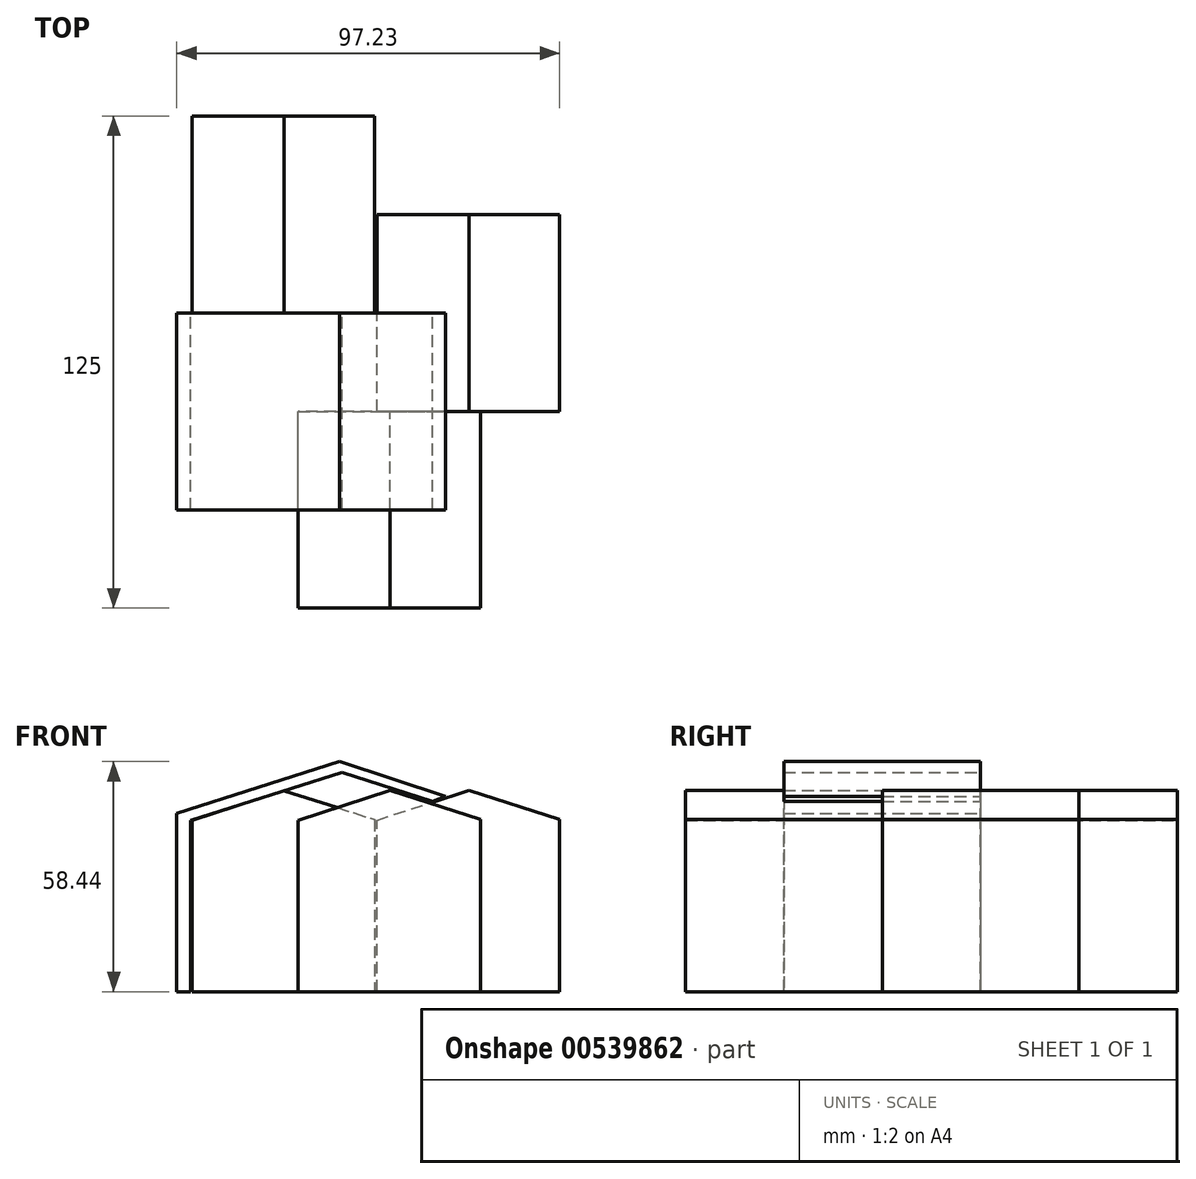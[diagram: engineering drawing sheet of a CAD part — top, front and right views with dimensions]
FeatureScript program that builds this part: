
annotation { "Feature Type Name" : "Feature", "Feature Type Description" : "" }
export const myFeature = defineFeature(function(context is Context, id is Id, definition is map)
    precondition{}
    {
        {
            var Q0;
            Q0=qCreatedBy(makeId("Front.planeOp"),FACE);
            var sketch = newSketch(context, id + "F0", { "sketchPlane" : qUnion([Q0])});
            skLineSegment(sketch, "E0", {"start": v(0, 0) * mm, "end": v(0, 43.57) * mm});
            skLineSegment(sketch, "E1", {"start": v(0, 43.57) * mm, "end": v(23.35, 51.09) * mm});
            skLineSegment(sketch, "E2", {"start": v(23.35, 51.09) * mm, "end": v(46.37, 43.73) * mm});
            skLineSegment(sketch, "E3", {"start": v(46.37, 43.73) * mm, "end": v(46.37, 0) * mm});
            skLineSegment(sketch, "E4", {"start": v(46.37, 0) * mm, "end": v(0, 0) * mm});
            skSolve(sketch);
        }
        {
            var Q0;
            Q0 = qSketchRegion(id + "F0", true);
            extrude(context, id + "F1", {"entities" : qUnion([Q0]), "depth" : 50 * mm, "offsetDistance" : 25 * mm});
        }
        {
            var Q0;
            Q0=makeQuery(id+"F1.opExtrude","SWEPT_BODY",BODY,{"disambiguationData":[OSD([sQuery(id+"F0.wireOp",EDGE,"E0"),sQuery(id+"F0.wireOp",EDGE,"E1"),sQuery(id+"F0.wireOp",EDGE,"E2"),sQuery(id+"F0.wireOp",EDGE,"E3"),sQuery(id+"F0.wireOp",EDGE,"E4")])]});
            transform(context, id + "F2", {"entities" : qUnion([Q0]), "transformType" : TransformType.TRANSLATION_3D, "dx" : 0 * mm, "dy" : 0 * mm, "dz" : 0 * mm, "makeCopy" : true});
        }
        {
            var Q0;
            Q0=makeQuery(id+"F2.opPattern","COPY",BODY,{"derivedFrom":makeQuery(id+"F1.opExtrude","SWEPT_BODY",BODY,{"disambiguationData":[OSD([sQuery(id+"F0.wireOp",EDGE,"E0"),sQuery(id+"F0.wireOp",EDGE,"E1"),sQuery(id+"F0.wireOp",EDGE,"E2"),sQuery(id+"F0.wireOp",EDGE,"E3"),sQuery(id+"F0.wireOp",EDGE,"E4")])]}),"instanceName":"1"});
            deleteBodies(context, id + "F3", {"entities" : qUnion([Q0])});
        }
        {
            var Q0;
            Q0=makeQuery(id+"F1.opExtrude","SWEPT_BODY",BODY,{"disambiguationData":[OSD([sQuery(id+"F0.wireOp",EDGE,"E0"),sQuery(id+"F0.wireOp",EDGE,"E1"),sQuery(id+"F0.wireOp",EDGE,"E2"),sQuery(id+"F0.wireOp",EDGE,"E3"),sQuery(id+"F0.wireOp",EDGE,"E4")])]});
            transform(context, id + "F4", {"entities" : qUnion([Q0]), "transformType" : TransformType.TRANSLATION_3D, "dx" : 20 * mm, "dy" : 50 * mm, "dz" : 0 * mm, "makeCopy" : true});
        }
        {
            var Q0;
            Q0=makeQuery(id+"F1.opExtrude","SWEPT_BODY",BODY,{"disambiguationData":[OSD([sQuery(id+"F0.wireOp",EDGE,"E0"),sQuery(id+"F0.wireOp",EDGE,"E1"),sQuery(id+"F0.wireOp",EDGE,"E2"),sQuery(id+"F0.wireOp",EDGE,"E3"),sQuery(id+"F0.wireOp",EDGE,"E4")])]});
            transform(context, id + "F5", {"entities" : qUnion([Q0]), "transformType" : TransformType.TRANSLATION_3D, "dx" : -27 * mm, "dy" : 75 * mm, "dz" : 0 * mm, "makeCopy" : true});
        }
        {
            var Q0;
            Q0=qCreatedBy(makeId("Front.planeOp"),FACE);
            var sketch = newSketch(context, id + "F6", { "sketchPlane" : qUnion([Q0])});
            skLineSegment(sketch, "E5", {"start": v(34.06, 48.37) * mm, "end": v(37.42, 49.65) * mm});
            skLineSegment(sketch, "E6", {"start": v(37.42, 49.65) * mm, "end": v(10.55, 58.44) * mm});
            skLineSegment(sketch, "E7", {"start": v(10.55, 58.44) * mm, "end": v(-30.86, 45.33) * mm});
            skLineSegment(sketch, "E8", {"start": v(-30.86, 45.33) * mm, "end": v(-30.86, 0) * mm});
            skLineSegment(sketch, "E9", {"start": v(-30.86, 0) * mm, "end": v(-27.34, 0) * mm});
            skLineSegment(sketch, "E10", {"start": v(-27.34, 0) * mm, "end": v(-27.34, 43.57) * mm});
            skLineSegment(sketch, "E11", {"start": v(-27.34, 43.57) * mm, "end": v(11.2, 55.72) * mm});
            skLineSegment(sketch, "E12", {"start": v(11.2, 55.72) * mm, "end": v(34.06, 48.37) * mm});
            skSolve(sketch);
        }
        {
            var Q0;
            Q0 = qSketchRegion(id + "F6", true);
            extrude(context, id + "F7", {"entities" : qUnion([Q0]), "operationType" : NewBodyOperationType.ADD, "endBound" : BoundingType.SYMMETRIC, "depth" : 50 * mm, "offsetDistance" : 25 * mm});
        }
    });
